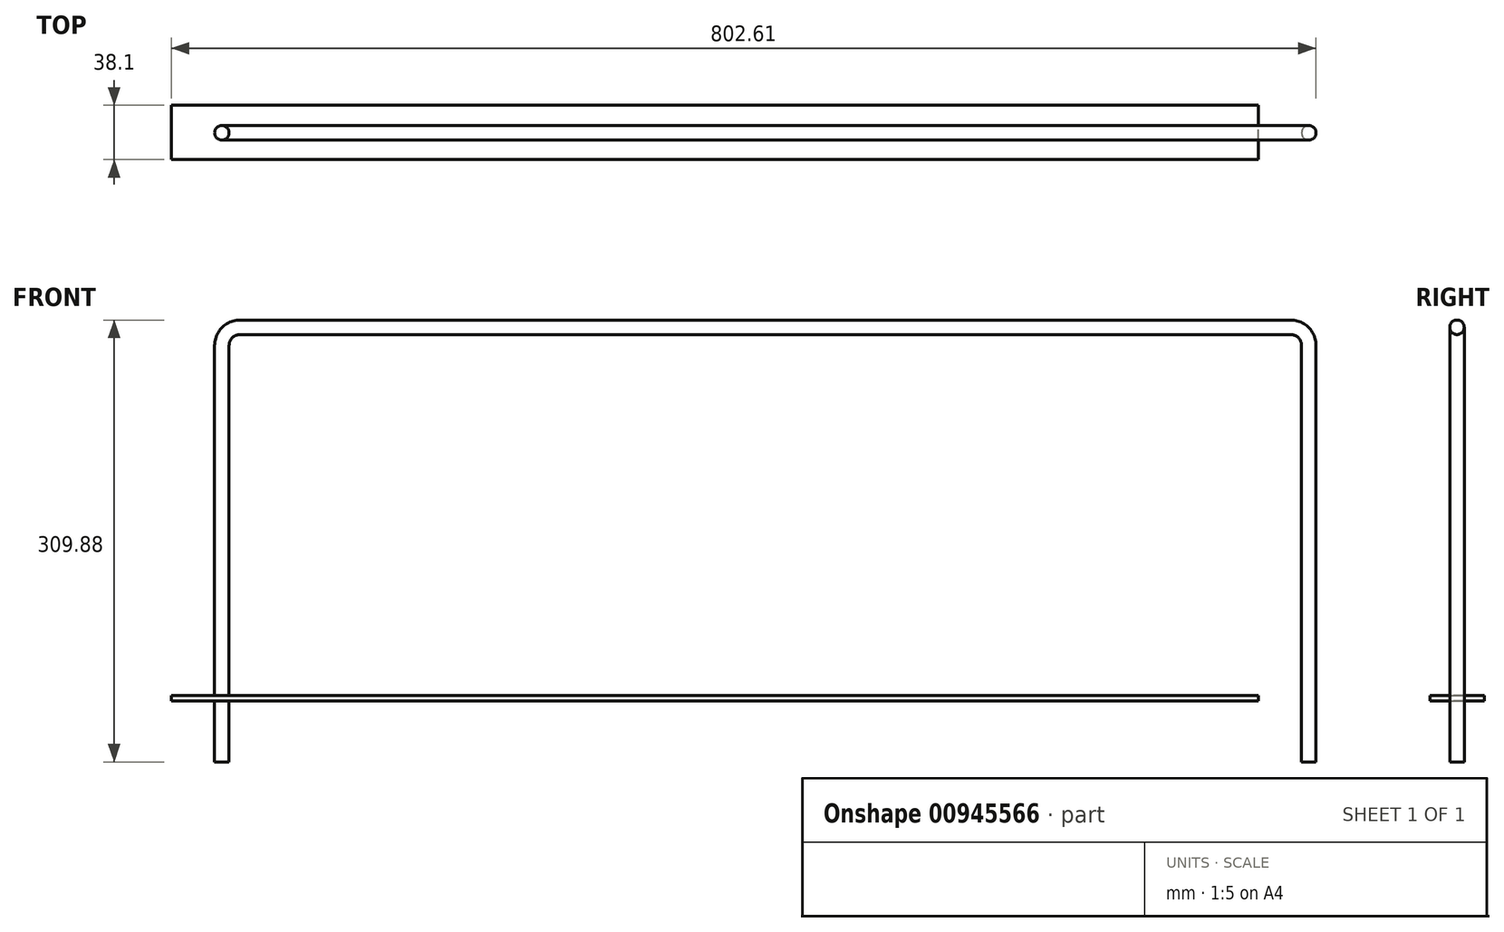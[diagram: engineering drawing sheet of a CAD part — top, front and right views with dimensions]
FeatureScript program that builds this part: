
annotation { "Feature Type Name" : "Feature", "Feature Type Description" : "" }
export const myFeature = defineFeature(function(context is Context, id is Id, definition is map)
    precondition{}
    {
        {
            var Q0;
            Q0=qCreatedBy(makeId("Front.planeOp"),FACE);
            var sketch = newSketch(context, id + "F0", { "sketchPlane" : qUnion([Q0])});
            skLineSegment(sketch, "E0", {"start": v(-345.47, 0) * mm, "end": v(-345.47, 292.1) * mm});
            skLineSegment(sketch, "E1", {"start": v(416.53, 0) * mm, "end": v(416.53, 292.1) * mm});
            skLineSegment(sketch, "E2", {"start": v(-332.77, 304.8) * mm, "end": v(403.83, 304.8) * mm});
            skArc(sketch, "E3", {"start": v(-332.77, 304.8) * mm, "mid": v(-341.75, 301.08) * mm, "end": v(-345.47, 292.1) * mm});
            skArc(sketch, "E4", {"start": v(416.53, 292.1) * mm, "mid": v(412.8, 301.08) * mm, "end": v(403.83, 304.8) * mm});
            skSolve(sketch);
        }
        {
            var Q0;
            Q0=qCreatedBy(makeId("Top.planeOp"),FACE);
            var sketch = newSketch(context, id + "F1", { "sketchPlane" : qUnion([Q0])});
            skCircle(sketch, "E5", {"center": v(-345.47, 0) * mm, "radius": 5.08 * mm});
            skSolve(sketch);
        }
        {
            var Q0;
            Q0=makeQuery(id+"F1.imprint","IMPRINT",FACE,{"disambiguationData":[TD([[makeQuery(id+"F1.imprint","IMPRINT",EDGE,{"derivedFrom":sQuery(id+"F1.wireOp",EDGE,"E5")}),1.0]])]});
            var Q1;
            Q1=sQuery(id+"F0.wireOp",EDGE,"E0");
            var Q2;
            Q2=sQuery(id+"F0.wireOp",EDGE,"E3");
            var Q3;
            Q3=sQuery(id+"F0.wireOp",EDGE,"E2");
            var Q4;
            Q4=sQuery(id+"F0.wireOp",EDGE,"E4");
            var Q5;
            Q5=sQuery(id+"F0.wireOp",EDGE,"E1");
            sweep(context, id + "F2", {"profiles" : qUnion([Q0]), "path" : qUnion([Q1, Q2, Q3, Q4, Q5])});
        }
        {
            var Q0;
            Q0=qCreatedBy(makeId("Right.planeOp"),FACE);
            var sketch = newSketch(context, id + "F3", { "sketchPlane" : qUnion([Q0])});
            skLineSegment(sketch, "E6.bottom", {"start": v(-18.78, 46.67) * mm, "end": v(19.32, 46.67) * mm});
            skLineSegment(sketch, "E6.top", {"start": v(-18.78, 42.86) * mm, "end": v(19.32, 42.86) * mm});
            skLineSegment(sketch, "E6.left", {"start": v(-18.78, 46.67) * mm, "end": v(-18.78, 42.86) * mm});
            skLineSegment(sketch, "E6.right", {"start": v(19.32, 46.67) * mm, "end": v(19.32, 42.86) * mm});
            skSolve(sketch);
        }
        {
            var Q0;
            Q0=makeQuery(id+"F3.imprint","IMPRINT",FACE,{"disambiguationData":[TD([[makeQuery(id+"F3.imprint","IMPRINT",EDGE,{"derivedFrom":sQuery(id+"F3.wireOp",EDGE,"E6.bottom")}),-1.0]])]});
            extrude(context, id + "F4", {"entities" : qUnion([Q0]), "operationType" : NewBodyOperationType.ADD, "endBound" : BoundingType.SYMMETRIC, "depth" : 762 * mm, "offsetDistance" : 25.4 * mm});
        }
    });
